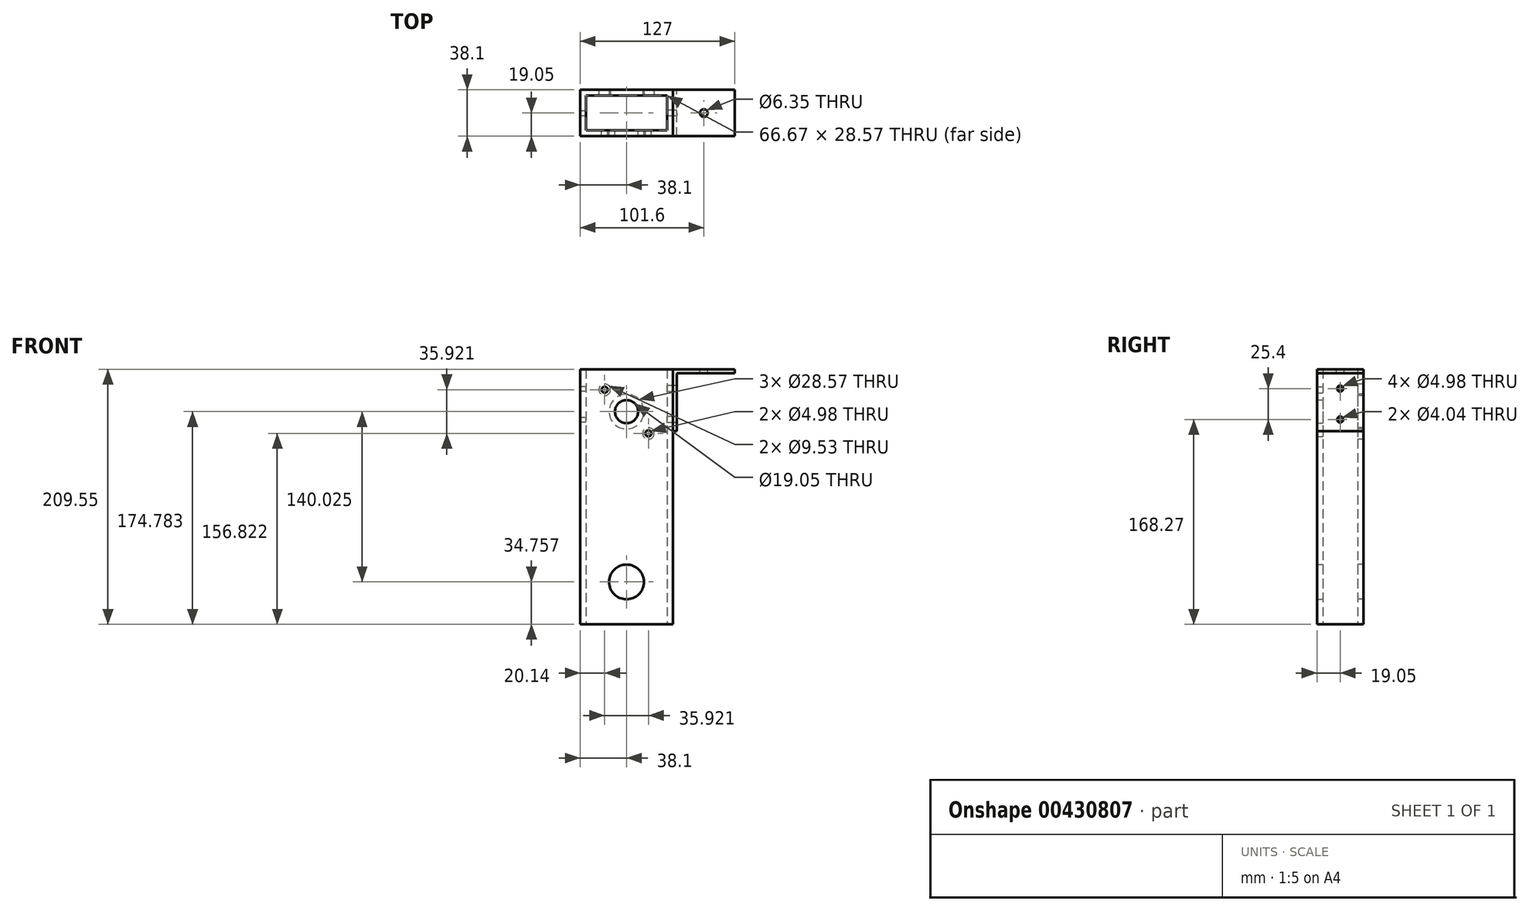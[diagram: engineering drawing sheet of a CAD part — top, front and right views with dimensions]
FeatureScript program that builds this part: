
annotation { "Feature Type Name" : "Feature", "Feature Type Description" : "" }
export const myFeature = defineFeature(function(context is Context, id is Id, definition is map)
    precondition{}
    {
        {
            var Q0;
            Q0=qCreatedBy(makeId("Top.planeOp"),FACE);
            var sketch = newSketch(context, id + "F0", { "sketchPlane" : qUnion([Q0])});
            skLineSegment(sketch, "E0.bottom", {"start": v(-38.1, 19.05) * mm, "end": v(38.1, 19.05) * mm});
            skLineSegment(sketch, "E0.top", {"start": v(-38.1, -19.05) * mm, "end": v(38.1, -19.05) * mm});
            skLineSegment(sketch, "E0.left", {"start": v(-38.1, 19.05) * mm, "end": v(-38.1, -19.05) * mm});
            skLineSegment(sketch, "E0.right", {"start": v(38.1, 19.05) * mm, "end": v(38.1, -19.05) * mm});
            skSolve(sketch);
        }
        {
            var Q0;
            Q0=makeQuery(id+"F0.imprint","IMPRINT",FACE,{"disambiguationData":[TD([[makeQuery(id+"F0.imprint","IMPRINT",EDGE,{"derivedFrom":sQuery(id+"F0.wireOp",EDGE,"E0.bottom")}),-1.0]])]});
            extrude(context, id + "F1", {"entities" : qUnion([Q0]), "depth" : 209.55 * mm, "symmetric" : true});
        }
        {
            var Q0;
            Q0=makeQuery(id+"F1.opExtrude","CAP_FACE",FACE,{"disambiguationData":[OSD([sQuery(id+"F0.wireOp",EDGE,"E0.bottom"),sQuery(id+"F0.wireOp",EDGE,"E0.top"),sQuery(id+"F0.wireOp",EDGE,"E0.left"),sQuery(id+"F0.wireOp",EDGE,"E0.right")])],"isStart":false});
            var Q1;
            Q1=makeQuery(id+"F1.opExtrude","CAP_FACE",FACE,{"disambiguationData":[OSD([sQuery(id+"F0.wireOp",EDGE,"E0.bottom"),sQuery(id+"F0.wireOp",EDGE,"E0.top"),sQuery(id+"F0.wireOp",EDGE,"E0.left"),sQuery(id+"F0.wireOp",EDGE,"E0.right")])],"isStart":true});
            shell(context, id + "F2", {"entities" : qUnion([Q0, Q1]), "thickness" : 4.76 * mm});
        }
        {
            var Q0;
            Q0=qCreatedBy(makeId("Front.planeOp"),FACE);
            var sketch = newSketch(context, id + "F3", { "sketchPlane" : qUnion([Q0])});
            skCircle(sketch, "E1", {"center": v(0, 70.01) * mm, "radius": 9.53 * mm});
            skCircle(sketch, "E2", {"center": v(0, -70.01) * mm, "radius": 14.29 * mm});
            skCircle(sketch, "E3", {"center": v(0, 70.01) * mm, "radius": 14.29 * mm});
            skCircle(sketch, "E4", {"center": v(-17.96, 87.97) * mm, "radius": 2.49 * mm});
            skCircle(sketch, "E5", {"center": v(17.96, 52.05) * mm, "radius": 2.49 * mm});
            skCircle(sketch, "E6", {"center": v(-17.96, 87.97) * mm, "radius": 4.76 * mm});
            skCircle(sketch, "E7", {"center": v(17.96, 52.05) * mm, "radius": 4.76 * mm});
            skCircle(sketch, "E8", {"center": v(0, 70.01) * mm, "radius": 25.4 * mm, "construction": true});
            skLineSegment(sketch, "E9", {"start": v(-17.96, 87.97) * mm, "end": v(17.96, 52.05) * mm, "construction": true});
            skSolve(sketch);
        }
        {
            var Q0;
            Q0=makeQuery(id+"F3.imprint","IMPRINT",FACE,{"disambiguationData":[TD([[makeQuery(id+"F3.imprint","IMPRINT",EDGE,{"derivedFrom":sQuery(id+"F3.wireOp",EDGE,"E1")}),1.0]])]});
            var Q1;
            Q1=makeQuery(id+"F3.imprint","IMPRINT",FACE,{"disambiguationData":[TD([[makeQuery(id+"F3.imprint","IMPRINT",EDGE,{"derivedFrom":sQuery(id+"F3.wireOp",EDGE,"E4")}),1.0]])]});
            var Q2;
            Q2=makeQuery(id+"F3.imprint","IMPRINT",FACE,{"disambiguationData":[TD([[makeQuery(id+"F3.imprint","IMPRINT",EDGE,{"derivedFrom":sQuery(id+"F3.wireOp",EDGE,"E5")}),1.0]])]});
            var Q3;
            Q3=makeQuery(id+"F3.imprint","IMPRINT",FACE,{"disambiguationData":[TD([[makeQuery(id+"F3.imprint","IMPRINT",EDGE,{"derivedFrom":sQuery(id+"F3.wireOp",EDGE,"E2")}),1.0]])]});
            extrude(context, id + "F4", {"entities" : qUnion([Q0, Q1, Q2, Q3]), "operationType" : NewBodyOperationType.REMOVE, "endBound" : BoundingType.THROUGH_ALL, "depth" : 25.4 * mm});
        }
        {
            var Q0;
            Q0=makeQuery(id+"F3.imprint","IMPRINT",FACE,{"disambiguationData":[TD([[makeQuery(id+"F3.imprint","IMPRINT",EDGE,{"derivedFrom":sQuery(id+"F3.wireOp",EDGE,"E4")}),-1.0]])]});
            var Q1;
            Q1=makeQuery(id+"F3.imprint","IMPRINT",FACE,{"disambiguationData":[TD([[makeQuery(id+"F3.imprint","IMPRINT",EDGE,{"derivedFrom":sQuery(id+"F3.wireOp",EDGE,"E4")}),1.0]])]});
            var Q2;
            Q2=makeQuery(id+"F3.imprint","IMPRINT",FACE,{"disambiguationData":[TD([[makeQuery(id+"F3.imprint","IMPRINT",EDGE,{"derivedFrom":sQuery(id+"F3.wireOp",EDGE,"E1")}),1.0]])]});
            var Q3;
            Q3=makeQuery(id+"F3.imprint","IMPRINT",FACE,{"disambiguationData":[TD([[makeQuery(id+"F3.imprint","IMPRINT",EDGE,{"derivedFrom":sQuery(id+"F3.wireOp",EDGE,"E1")}),-1.0]])]});
            var Q4;
            Q4=makeQuery(id+"F3.imprint","IMPRINT",FACE,{"disambiguationData":[TD([[makeQuery(id+"F3.imprint","IMPRINT",EDGE,{"derivedFrom":sQuery(id+"F3.wireOp",EDGE,"E5")}),1.0]])]});
            var Q5;
            Q5=makeQuery(id+"F3.imprint","IMPRINT",FACE,{"disambiguationData":[TD([[makeQuery(id+"F3.imprint","IMPRINT",EDGE,{"derivedFrom":sQuery(id+"F3.wireOp",EDGE,"E5")}),-1.0]])]});
            var Q6;
            Q6=makeQuery(id+"F3.imprint","IMPRINT",FACE,{"disambiguationData":[TD([[makeQuery(id+"F3.imprint","IMPRINT",EDGE,{"derivedFrom":sQuery(id+"F3.wireOp",EDGE,"E2")}),1.0]])]});
            extrude(context, id + "F5", {"entities" : qUnion([Q0, Q1, Q2, Q3, Q4, Q5, Q6]), "operationType" : NewBodyOperationType.REMOVE, "oppositeDirection" : true, "depth" : 25.4 * mm});
        }
        {
            var Q0;
            Q0=qCreatedBy(makeId("Front.planeOp"),FACE);
            var sketch = newSketch(context, id + "F6", { "sketchPlane" : qUnion([Q0])});
            skLineSegment(sketch, "E10", {"start": v(38.1, 53.98) * mm, "end": v(38.1, 104.78) * mm});
            skLineSegment(sketch, "E11", {"start": v(38.1, 104.78) * mm, "end": v(88.9, 104.78) * mm});
            skLineSegment(sketch, "E12", {"start": v(88.9, 104.78) * mm, "end": v(88.9, 101.6) * mm});
            skLineSegment(sketch, "E13", {"start": v(88.9, 101.6) * mm, "end": v(41.28, 101.6) * mm});
            skLineSegment(sketch, "E14", {"start": v(41.28, 101.6) * mm, "end": v(41.28, 53.98) * mm});
            skLineSegment(sketch, "E15", {"start": v(41.28, 53.98) * mm, "end": v(38.1, 53.98) * mm});
            skSolve(sketch);
        }
        {
            var Q0;
            Q0=makeQuery(id+"F6.imprint","IMPRINT",FACE,{"disambiguationData":[TD([[makeQuery(id+"F6.imprint","IMPRINT",EDGE,{"derivedFrom":sQuery(id+"F6.wireOp",EDGE,"E10")}),-1.0]])]});
            extrude(context, id + "F7", {"entities" : qUnion([Q0]), "depth" : 38.1 * mm, "symmetric" : true});
        }
        {
            var Q0;
            Q0=qCreatedBy(makeId("Right.planeOp"),FACE);
            var sketch = newSketch(context, id + "F8", { "sketchPlane" : qUnion([Q0])});
            skCircle(sketch, "E16", {"center": v(0, 88.9) * mm, "radius": 2.02 * mm});
            skCircle(sketch, "E17", {"center": v(0, 63.5) * mm, "radius": 2.02 * mm});
            skCircle(sketch, "E18", {"center": v(0, 88.9) * mm, "radius": 2.49 * mm});
            skCircle(sketch, "E19", {"center": v(0, 63.5) * mm, "radius": 2.49 * mm});
            skSolve(sketch);
        }
        {
            var Q0;
            Q0=makeQuery(id+"F8.imprint","IMPRINT",FACE,{"disambiguationData":[TD([[makeQuery(id+"F8.imprint","IMPRINT",EDGE,{"derivedFrom":sQuery(id+"F8.wireOp",EDGE,"E16")}),1.0]])]});
            var Q1;
            Q1=makeQuery(id+"F8.imprint","IMPRINT",FACE,{"disambiguationData":[TD([[makeQuery(id+"F8.imprint","IMPRINT",EDGE,{"derivedFrom":sQuery(id+"F8.wireOp",EDGE,"E17")}),1.0]])]});
            extrude(context, id + "F9", {"entities" : qUnion([Q0, Q1]), "operationType" : NewBodyOperationType.REMOVE, "endBound" : BoundingType.THROUGH_ALL, "oppositeDirection" : true, "depth" : 25.4 * mm, "hasSecondDirection" : true, "secondDirectionBound" : BoundingType.THROUGH_ALL, "secondDirectionOppositeDirection" : false, "secondDirectionDepth" : 25.4 * mm});
        }
        {
            var Q0;
            Q0=makeQuery(id+"F7.opExtrude","SWEPT_FACE",FACE,{"disambiguationData":[OSD([sQuery(id+"F6.wireOp",EDGE,"E11")])]});
            var sketch = newSketch(context, id + "F10", { "sketchPlane" : qUnion([Q0])});
            skCircle(sketch, "E20", {"center": v(63.5, 0) * mm, "radius": 3.18 * mm});
            skPoint(sketch, "E20.centerSnap0", {"position": v(63.5, -19.05) * mm});
            skPoint(sketch, "E20.centerSnap1", {"position": v(88.9, 0) * mm});
            skSolve(sketch);
        }
        {
            var Q0;
            Q0=makeQuery(id+"F10.imprint","IMPRINT",FACE,{"disambiguationData":[TD([[makeQuery(id+"F10.imprint","IMPRINT",EDGE,{"derivedFrom":sQuery(id+"F10.wireOp",EDGE,"E20")}),1.0]])]});
            extrude(context, id + "F11", {"entities" : qUnion([Q0]), "operationType" : NewBodyOperationType.REMOVE, "endBound" : BoundingType.THROUGH_ALL, "oppositeDirection" : true, "depth" : 25.4 * mm});
        }
        {
            var Q0;
            Q0=makeQuery(id+"F8.imprint","IMPRINT",FACE,{"disambiguationData":[TD([[makeQuery(id+"F8.imprint","IMPRINT",EDGE,{"derivedFrom":sQuery(id+"F8.wireOp",EDGE,"E16")}),1.0]])]});
            var Q1;
            Q1=makeQuery(id+"F8.imprint","IMPRINT",FACE,{"disambiguationData":[TD([[makeQuery(id+"F8.imprint","IMPRINT",EDGE,{"derivedFrom":sQuery(id+"F8.wireOp",EDGE,"E16")}),-1.0]])]});
            var Q2;
            Q2=makeQuery(id+"F8.imprint","IMPRINT",FACE,{"disambiguationData":[TD([[makeQuery(id+"F8.imprint","IMPRINT",EDGE,{"derivedFrom":sQuery(id+"F8.wireOp",EDGE,"E17")}),1.0]])]});
            var Q3;
            Q3=makeQuery(id+"F8.imprint","IMPRINT",FACE,{"disambiguationData":[TD([[makeQuery(id+"F8.imprint","IMPRINT",EDGE,{"derivedFrom":sQuery(id+"F8.wireOp",EDGE,"E17")}),-1.0]])]});
            extrude(context, id + "F12", {"entities" : qUnion([Q0, Q1, Q2, Q3]), "operationType" : NewBodyOperationType.REMOVE, "endBound" : BoundingType.THROUGH_ALL, "depth" : 25.4 * mm});
        }
    });
